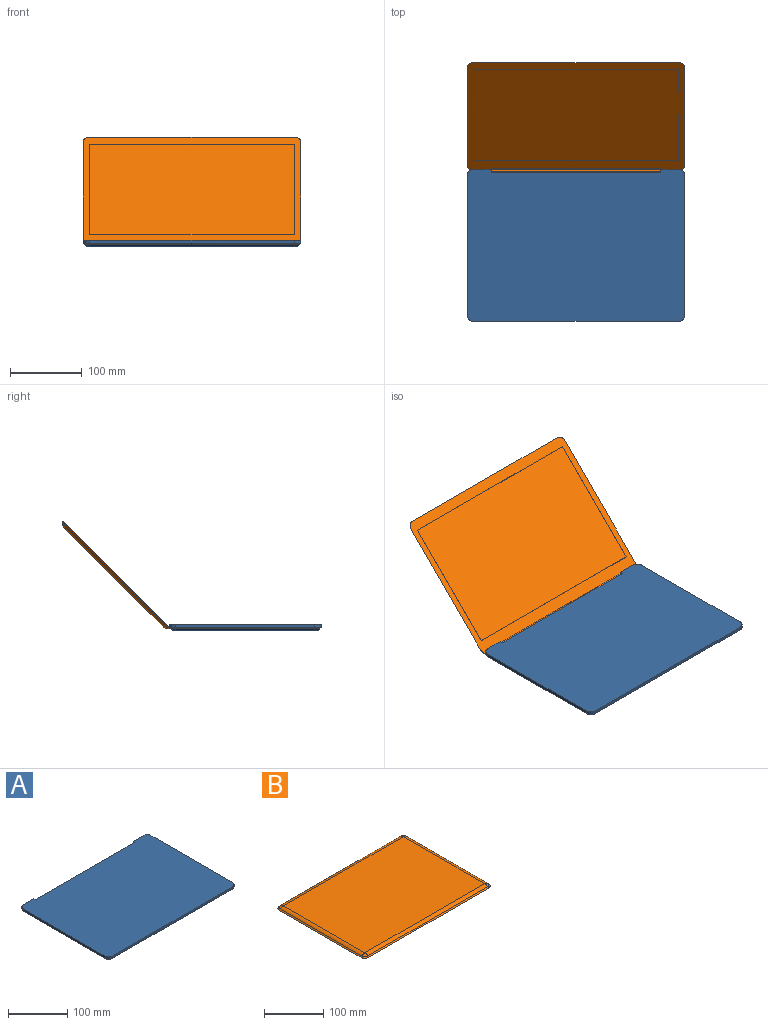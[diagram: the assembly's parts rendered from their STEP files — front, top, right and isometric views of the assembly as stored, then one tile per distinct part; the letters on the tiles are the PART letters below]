
ASSEMBLY  parts=2 mates=1
PART A: 31 faces, bbox 304.1x212.4x9.4 mm
  f0: plane 24.55x4.4mm, normal (0,1,0), area 108mm2, adj f1,f2,f10,f30
  f1: plane 24.55x2.07mm, normal (0,0.71,-0.71), area 71.9mm2, adj f0,f16,f26,f30
  f2: cylinder r=9mm len=9mm, axis (0,0,-1), area 62.2mm2, adj f0,f9,f10,f16
  f3: plane 24.55x4.4mm, normal (0,1,0), area 108mm2, adj f4,f10,f14,f28
  f4: cylinder r=9mm len=9mm, axis (0,0,-1), area 62.2mm2, adj f3,f5,f10,f12
  f5: plane 194.4x4.4mm, normal (-1,0,0), area 855.4mm2, adj f4,f6,f10,f13
  f6: cylinder r=9mm len=9mm, axis (0,0,-1), area 62.2mm2, adj f5,f7,f10,f15
  f7: plane 286.1x4.4mm, normal (0,-1,0), area 1258.8mm2, adj f6,f8,f10,f17
  f8: cylinder r=9mm len=9mm, axis (0,0,-1), area 62.2mm2, adj f7,f9,f10,f19
  f9: plane 194.4x4.4mm, normal (1,0,0), area 855.4mm2, adj f2,f8,f10,f18
  f10: plane 304.1x212.4mm, normal (0,0,1), area 63573.3mm2, adj f0,f2,f3,f4,f5,f6,f7,f8
  f11: plane 285.82x194.12mm, normal (0,0,-1), area 55481.3mm2, adj f21,f22,f25,f26
  f12: cone r=9mm half-angle=45deg, axis (0,0,1), area 36.6mm2, adj f4,f13,f14,f27
  f13: plane 194.4x2.07mm, normal (-0.71,0,-0.71), area 569.4mm2, adj f5,f12,f15,f25
  f14: plane 24.55x2.07mm, normal (0,0.71,-0.71), area 71.9mm2, adj f3,f12,f26,f28
  f15: cone r=9mm half-angle=45deg, axis (0,0,1), area 36.6mm2, adj f6,f13,f17,f23
  f16: cone r=9mm half-angle=45deg, axis (0,0,1), area 36.6mm2, adj f1,f2,f18,f24
  f17: plane 286.1x2.07mm, normal (0,-0.71,-0.71), area 838mm2, adj f7,f15,f19,f21
  f18: plane 194.4x2.07mm, normal (0.71,0,-0.71), area 569.4mm2, adj f9,f16,f19,f22
  f19: cone r=9mm half-angle=45deg, axis (0,0,1), area 36.6mm2, adj f8,f17,f18,f20
  f20: bspline ~7.07x7.07mm, area 44.9mm2, adj f19,f21,f22
  f21: cylinder r=10mm len=286.1mm, axis (1,0,0), area 2245.9mm2, adj f11,f17,f20,f23
  f22: cylinder r=10mm len=194.4mm, axis (0,-1,0), area 1525.7mm2, adj f11,f18,f20,f24
  f23: bspline ~7.07x7.07mm, area 44.9mm2, adj f15,f21,f25
  f24: bspline ~7.07x7.07mm, area 44.9mm2, adj f16,f22,f26
  f25: cylinder r=10mm len=194.4mm, axis (0,-1,0), area 1525.7mm2, adj f11,f13,f23,f27
  f26: cylinder r=10mm len=286.1mm, axis (1,0,0), area 1664.6mm2, adj f1,f11,f14,f24,f27,f28,f29,f30
  f27: bspline ~7.07x7.07mm, area 44.9mm2, adj f12,f25,f26
  f28: plane 7.98x4mm, normal (1,0,0), area 25.3mm2, adj f3,f10,f14,f26,f29
  f29: plane 237x7.98mm, normal (0,1,0), area 1890.5mm2, adj f10,f26,f28,f30
  f30: plane 7.98x4mm, normal (-1,0,0), area 25.3mm2, adj f0,f1,f10,f26,f29
PART B: 29 faces, bbox 304.1x212.4x10 mm
  f0: plane 304.1x212.4mm, normal (0,0,-1), area 12647.5mm2, adj f3,f4,f5,f6,f8,f9,f10,f13
  f1: plane 237x5mm, normal (0,1,0), area 1185mm2, adj f8,f10,f11,f15
  f2: plane 285.82x194.12mm, normal (0,0,1), area 55481.3mm2, adj f22,f23,f26,f27
  f3: plane 286.1x0.25mm, normal (0,1,0), area 71.5mm2, adj f0,f4,f6,f7
  f4: plane 178x0.25mm, normal (-1,0,0), area 44.5mm2, adj f0,f3,f5,f7
  f5: plane 286.1x0.25mm, normal (0,-1,0), area 71.5mm2, adj f0,f4,f6,f7
  f6: plane 178x0.25mm, normal (1,0,0), area 44.5mm2, adj f0,f3,f5,f7
  f7: plane 286.1x178mm, normal (0,0,-1), area 50925.8mm2, adj f3,f4,f5,f6
  f8: plane 5x4mm, normal (-1,0,0), area 19.1mm2, adj f0,f1,f9,f11,f12
  f9: plane 237x3mm, normal (0,-1,0), area 711mm2, adj f0,f8,f10,f12
  f10: plane 5x4mm, normal (1,0,0), area 19.1mm2, adj f0,f1,f9,f11,f12
  f11: plane 237x2mm, normal (0,0,-1), area 474mm2, adj f1,f8,f10,f12
  f12: cylinder r=2mm len=237mm, axis (-1,0,0), area 744.6mm2, adj f8,f9,f10,f11
  f13: cone r=4mm half-angle=45deg, axis (0,0,-1), area 36.6mm2, adj f0,f14,f15,f25
  f14: plane 194.4x2.07mm, normal (-0.71,0,0.71), area 569.4mm2, adj f0,f13,f16,f23
  f15: plane 286.1x2.07mm, normal (0,0.71,0.71), area 838mm2, adj f0,f1,f13,f17,f27
  f16: cone r=4mm half-angle=45deg, axis (0,0,-1), area 36.6mm2, adj f0,f14,f18,f21
  f17: cone r=4mm half-angle=45deg, axis (0,0,-1), area 36.6mm2, adj f0,f15,f19,f28
  f18: plane 286.1x2.07mm, normal (0,-0.71,0.71), area 838mm2, adj f0,f16,f20,f22
  f19: plane 194.4x2.07mm, normal (0.71,0,0.71), area 569.4mm2, adj f0,f17,f20,f26
  f20: cone r=4mm half-angle=45deg, axis (0,0,-1), area 36.6mm2, adj f0,f18,f19,f24
  f21: bspline ~7.07x7.07mm, area 44.9mm2, adj f16,f22,f23
  f22: cylinder r=10mm len=286.1mm, axis (-1,0,0), area 2245.9mm2, adj f2,f18,f21,f24
  f23: cylinder r=10mm len=194.4mm, axis (0,1,0), area 1525.7mm2, adj f2,f14,f21,f25
  f24: bspline ~7.07x7.07mm, area 44.9mm2, adj f20,f22,f26
  f25: bspline ~7.07x7.07mm, area 44.9mm2, adj f13,f23,f27
  f26: cylinder r=10mm len=194.4mm, axis (0,1,0), area 1525.7mm2, adj f2,f19,f24,f28
  f27: cylinder r=10mm len=286.1mm, axis (-1,0,0), area 2245.9mm2, adj f2,f15,f25,f28
  f28: bspline ~7.07x7.07mm, area 44.9mm2, adj f17,f26,f27
PLACE A at identity fixed
PLACE B rot(axis=(-1,0,0),135deg) t=(0,180,77.96)mm
MATE revolute B.f12 <-> A.f28  axis (-1,0,0) through (-118.5,104.2,6.4)mm
